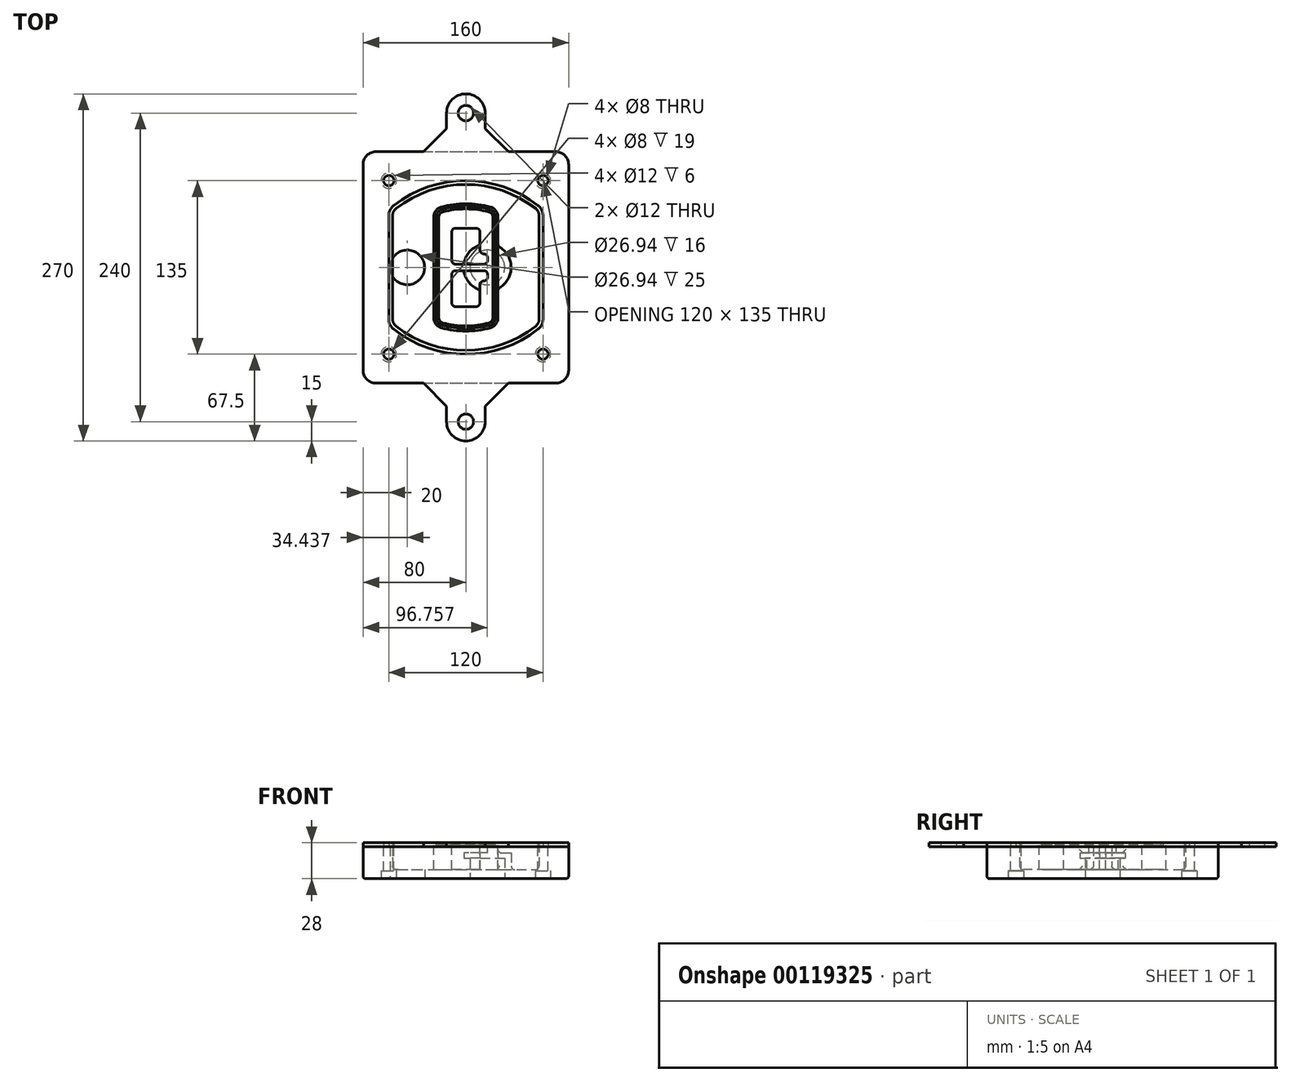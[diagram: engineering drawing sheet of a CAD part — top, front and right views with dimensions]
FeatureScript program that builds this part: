
annotation { "Feature Type Name" : "Feature", "Feature Type Description" : "" }
export const myFeature = defineFeature(function(context is Context, id is Id, definition is map)
    precondition{}
    {
        {
            var Q0;
            Q0=qCreatedBy(makeId("Top.planeOp"),FACE);
            var sketch = newSketch(context, id + "F0", { "sketchPlane" : qUnion([Q0])});
            skPoint(sketch, "E0.rect.middle", {"position": v(0, 0) * mm});
            skLineSegment(sketch, "E1.bottom", {"start": v(-70, -90) * mm, "end": v(70, -90) * mm});
            skLineSegment(sketch, "E1.top", {"start": v(-70, 90) * mm, "end": v(70, 90) * mm});
            skLineSegment(sketch, "E1.left", {"start": v(-80, -80) * mm, "end": v(-80, 80) * mm});
            skLineSegment(sketch, "E1.right", {"start": v(80, -80) * mm, "end": v(80, 80) * mm});
            skLineSegment(sketch, "E2", {"start": v(-80, 90) * mm, "end": v(80, -90) * mm, "construction": true});
            skLineSegment(sketch, "E3", {"start": v(80, 90) * mm, "end": v(-80, -90) * mm, "construction": true});
            skCircle(sketch, "E4", {"center": v(-60, 67.5) * mm, "radius": 4 * mm});
            skCircle(sketch, "E5", {"center": v(60, 67.5) * mm, "radius": 4 * mm});
            skCircle(sketch, "E6", {"center": v(60, -67.5) * mm, "radius": 4 * mm});
            skCircle(sketch, "E7", {"center": v(-60, -67.5) * mm, "radius": 4 * mm});
            skLineSegment(sketch, "E8", {"start": v(-60, 67.5) * mm, "end": v(60, 67.5) * mm, "construction": true});
            skLineSegment(sketch, "E9", {"start": v(60, 67.5) * mm, "end": v(60, -67.5) * mm, "construction": true});
            skLineSegment(sketch, "E10", {"start": v(60, -67.5) * mm, "end": v(-60, -67.5) * mm, "construction": true});
            skLineSegment(sketch, "E11", {"start": v(-60, -67.5) * mm, "end": v(-60, 67.5) * mm, "construction": true});
            skLineSegment(sketch, "E12", {"start": v(-60, 40.3) * mm, "end": v(-60, -40.3) * mm});
            skLineSegment(sketch, "E13", {"start": v(60, 40.3) * mm, "end": v(60, -40.3) * mm});
            skArc(sketch, "E14", {"start": v(56.15, 48.18) * mm, "mid": v(0, 67.5) * mm, "end": v(-56.15, 48.18) * mm});
            skArc(sketch, "E15", {"start": v(-56.15, -48.18) * mm, "mid": v(0, -67.5) * mm, "end": v(56.15, -48.18) * mm});
            skLineSegment(sketch, "E16", {"start": v(-60, 0) * mm, "end": v(60, 0) * mm, "construction": true});
            skPoint(sketch, "E17.visualSharp", {"position": v(-60, -45) * mm});
            skArc(sketch, "E17.filletArc", {"start": v(-60, -40.3) * mm, "mid": v(-58.99, -44.68) * mm, "end": v(-56.15, -48.18) * mm});
            skPoint(sketch, "E18.visualSharp", {"position": v(-60, 45) * mm});
            skArc(sketch, "E18.filletArc", {"start": v(-56.15, 48.18) * mm, "mid": v(-58.99, 44.68) * mm, "end": v(-60, 40.3) * mm});
            skPoint(sketch, "E19.visualSharp", {"position": v(60, 45) * mm});
            skArc(sketch, "E19.filletArc", {"start": v(60, 40.3) * mm, "mid": v(58.99, 44.68) * mm, "end": v(56.15, 48.18) * mm});
            skPoint(sketch, "E20.visualSharp", {"position": v(60, -45) * mm});
            skArc(sketch, "E20.filletArc", {"start": v(56.15, -48.18) * mm, "mid": v(58.99, -44.68) * mm, "end": v(60, -40.3) * mm});
            skPoint(sketch, "E21.visualSharp", {"position": v(-80, 90) * mm});
            skArc(sketch, "E21.filletArc", {"start": v(-70, 90) * mm, "mid": v(-77.07, 87.07) * mm, "end": v(-80, 80) * mm});
            skPoint(sketch, "E22.visualSharp", {"position": v(80, 90) * mm});
            skArc(sketch, "E22.filletArc", {"start": v(80, 80) * mm, "mid": v(77.07, 87.07) * mm, "end": v(70, 90) * mm});
            skPoint(sketch, "E23.visualSharp", {"position": v(80, -90) * mm});
            skArc(sketch, "E23.filletArc", {"start": v(70, -90) * mm, "mid": v(77.07, -87.07) * mm, "end": v(80, -80) * mm});
            skPoint(sketch, "E24.visualSharp", {"position": v(-80, -90) * mm});
            skArc(sketch, "E24.filletArc", {"start": v(-80, -80) * mm, "mid": v(-77.07, -87.07) * mm, "end": v(-70, -90) * mm});
            skArc(sketch, "E25.0", {"start": v(57, 40.3) * mm, "mid": v(56.3, 43.36) * mm, "end": v(54.3, 45.81) * mm});
            skLineSegment(sketch, "E25.1", {"start": v(57, 40.3) * mm, "end": v(57, -40.3) * mm});
            skArc(sketch, "E25.2", {"start": v(54.3, -45.81) * mm, "mid": v(56.3, -43.36) * mm, "end": v(57, -40.3) * mm});
            skArc(sketch, "E25.3", {"start": v(-54.3, -45.81) * mm, "mid": v(0, -64.5) * mm, "end": v(54.3, -45.81) * mm});
            skArc(sketch, "E25.4", {"start": v(-57, -40.3) * mm, "mid": v(-56.3, -43.36) * mm, "end": v(-54.3, -45.81) * mm});
            skArc(sketch, "E25.5", {"start": v(54.3, 45.81) * mm, "mid": v(0, 64.5) * mm, "end": v(-54.3, 45.81) * mm});
            skLineSegment(sketch, "E25.6", {"start": v(-57, 40.3) * mm, "end": v(-57, -40.3) * mm});
            skArc(sketch, "E25.7", {"start": v(-54.3, 45.81) * mm, "mid": v(-56.3, 43.36) * mm, "end": v(-57, 40.3) * mm});
            skArc(sketch, "E26.0", {"start": v(-58.62, 51.33) * mm, "mid": v(-62.58, 46.43) * mm, "end": v(-64, 40.3) * mm});
            skArc(sketch, "E26.1", {"start": v(58.62, 51.33) * mm, "mid": v(0, 71.5) * mm, "end": v(-58.62, 51.33) * mm});
            skArc(sketch, "E26.2", {"start": v(64, 40.3) * mm, "mid": v(62.58, 46.43) * mm, "end": v(58.62, 51.33) * mm});
            skLineSegment(sketch, "E26.3", {"start": v(64, 40.3) * mm, "end": v(64, -40.3) * mm});
            skArc(sketch, "E26.4", {"start": v(58.62, -51.33) * mm, "mid": v(62.58, -46.43) * mm, "end": v(64, -40.3) * mm});
            skLineSegment(sketch, "E26.5", {"start": v(-64, 40.3) * mm, "end": v(-64, -40.3) * mm});
            skArc(sketch, "E26.6", {"start": v(-58.62, -51.33) * mm, "mid": v(0, -71.5) * mm, "end": v(58.62, -51.33) * mm});
            skArc(sketch, "E26.7", {"start": v(-64, -40.3) * mm, "mid": v(-62.58, -46.43) * mm, "end": v(-58.62, -51.33) * mm});
            skSolve(sketch);
        }
        {
            var Q0;
            Q0=makeQuery(id+"F0.imprint","IMPRINT",FACE,{"disambiguationData":[TD([[makeQuery(id+"F0.imprint","IMPRINT",EDGE,{"derivedFrom":sQuery(id+"F0.wireOp",EDGE,"E1.bottom")}),1.0]])]});
            var Q1;
            Q1=makeQuery(id+"F0.imprint","IMPRINT",FACE,{"disambiguationData":[TD([[makeQuery(id+"F0.imprint","IMPRINT",EDGE,{"derivedFrom":sQuery(id+"F0.wireOp",EDGE,"E12")}),1.0]])]});
            var Q2;
            Q2=makeQuery(id+"F0.imprint","IMPRINT",FACE,{"disambiguationData":[TD([[makeQuery(id+"F0.imprint","IMPRINT",EDGE,{"derivedFrom":sQuery(id+"F0.wireOp",EDGE,"E25.0")}),1.0]])]});
            var Q3;
            Q3=makeQuery(id+"F0.imprint","IMPRINT",FACE,{"disambiguationData":[TD([[makeQuery(id+"F0.imprint","IMPRINT",EDGE,{"derivedFrom":sQuery(id+"F0.wireOp",EDGE,"E12")}),-1.0]])]});
            extrude(context, id + "F1", {"entities" : qUnion([Q0, Q1, Q2, Q3]), "oppositeDirection" : true, "depth" : 25 * mm});
        }
        {
            var Q0;
            Q0=makeQuery(id+"F0.imprint","IMPRINT",FACE,{"disambiguationData":[TD([[makeQuery(id+"F0.imprint","IMPRINT",EDGE,{"derivedFrom":sQuery(id+"F0.wireOp",EDGE,"E12")}),1.0]])]});
            extrude(context, id + "F2", {"entities" : qUnion([Q0]), "operationType" : NewBodyOperationType.ADD, "depth" : 3 * mm});
        }
        {
            var Q0;
            Q0=makeQuery(id+"F0.imprint","IMPRINT",FACE,{"disambiguationData":[TD([[makeQuery(id+"F0.imprint","IMPRINT",EDGE,{"derivedFrom":sQuery(id+"F0.wireOp",EDGE,"E25.0")}),1.0]])]});
            extrude(context, id + "F3", {"entities" : qUnion([Q0]), "operationType" : NewBodyOperationType.REMOVE, "oppositeDirection" : true, "depth" : 18 * mm});
        }
        {
            var Q0;
            Q0=makeQuery(id+"F2.opExtrude","CAP_FACE",FACE,{"disambiguationData":[OSD([sQuery(id+"F0.wireOp",EDGE,"E12"),sQuery(id+"F0.wireOp",EDGE,"E13"),sQuery(id+"F0.wireOp",EDGE,"E14"),sQuery(id+"F0.wireOp",EDGE,"E15"),sQuery(id+"F0.wireOp",EDGE,"E17.filletArc"),sQuery(id+"F0.wireOp",EDGE,"E18.filletArc"),sQuery(id+"F0.wireOp",EDGE,"E19.filletArc"),sQuery(id+"F0.wireOp",EDGE,"E20.filletArc"),sQuery(id+"F0.wireOp",EDGE,"E25.0"),sQuery(id+"F0.wireOp",EDGE,"E25.1"),sQuery(id+"F0.wireOp",EDGE,"E25.2"),sQuery(id+"F0.wireOp",EDGE,"E25.3"),sQuery(id+"F0.wireOp",EDGE,"E25.4"),sQuery(id+"F0.wireOp",EDGE,"E25.5"),sQuery(id+"F0.wireOp",EDGE,"E25.6"),sQuery(id+"F0.wireOp",EDGE,"E25.7")])],"isStart":false});
            var sketch = newSketch(context, id + "F4", { "sketchPlane" : qUnion([Q0])});
            skArc(sketch, "E27.0", {"start": v(-19.08, -46.97) * mm, "mid": v(0, -49.5) * mm, "end": v(19.08, -46.97) * mm});
            skArc(sketch, "E28.0", {"start": v(19.08, 46.97) * mm, "mid": v(0, 49.5) * mm, "end": v(-19.08, 46.97) * mm});
            skLineSegment(sketch, "E29", {"start": v(-25, 39.25) * mm, "end": v(-25, -39.25) * mm});
            skLineSegment(sketch, "E30", {"start": v(25, 39.25) * mm, "end": v(25, -39.25) * mm});
            skLineSegment(sketch, "E31", {"start": v(-25, 45.1) * mm, "end": v(25, 45.1) * mm, "construction": true});
            skLineSegment(sketch, "E32", {"start": v(-25, -45.1) * mm, "end": v(25, -45.1) * mm, "construction": true});
            skPoint(sketch, "E33.visualSharp", {"position": v(-25, 45.1) * mm});
            skArc(sketch, "E33.filletArc", {"start": v(-19.08, 46.97) * mm, "mid": v(-23.35, 44.11) * mm, "end": v(-25, 39.25) * mm});
            skPoint(sketch, "E34.visualSharp", {"position": v(25, 45.1) * mm});
            skArc(sketch, "E34.filletArc", {"start": v(25, 39.25) * mm, "mid": v(23.35, 44.11) * mm, "end": v(19.08, 46.97) * mm});
            skPoint(sketch, "E35.visualSharp", {"position": v(25, -45.1) * mm});
            skArc(sketch, "E35.filletArc", {"start": v(19.08, -46.97) * mm, "mid": v(23.35, -44.11) * mm, "end": v(25, -39.25) * mm});
            skPoint(sketch, "E36.visualSharp", {"position": v(-25, -45.1) * mm});
            skArc(sketch, "E36.filletArc", {"start": v(-25, -39.25) * mm, "mid": v(-23.35, -44.11) * mm, "end": v(-19.08, -46.97) * mm});
            skArc(sketch, "E37.0", {"start": v(54.3, 45.81) * mm, "mid": v(0, 64.5) * mm, "end": v(-54.3, 45.81) * mm});
            skArc(sketch, "E37.1", {"start": v(-54.3, 45.81) * mm, "mid": v(-56.3, 43.36) * mm, "end": v(-57, 40.3) * mm});
            skLineSegment(sketch, "E37.2", {"start": v(-57, 40.3) * mm, "end": v(-57, -40.3) * mm});
            skArc(sketch, "E37.3", {"start": v(-57, -40.3) * mm, "mid": v(-56.3, -43.36) * mm, "end": v(-54.3, -45.81) * mm});
            skArc(sketch, "E37.4", {"start": v(-54.3, -45.81) * mm, "mid": v(0, -64.5) * mm, "end": v(54.3, -45.81) * mm});
            skArc(sketch, "E37.5", {"start": v(54.3, -45.81) * mm, "mid": v(56.3, -43.36) * mm, "end": v(57, -40.3) * mm});
            skLineSegment(sketch, "E37.6", {"start": v(57, 40.3) * mm, "end": v(57, -40.3) * mm});
            skArc(sketch, "E37.7", {"start": v(57, 40.3) * mm, "mid": v(56.3, 43.36) * mm, "end": v(54.3, 45.81) * mm});
            skLineSegment(sketch, "E38.0", {"start": v(23, 39.25) * mm, "end": v(23, -39.25) * mm});
            skArc(sketch, "E38.1", {"start": v(18.56, -45.04) * mm, "mid": v(21.76, -42.9) * mm, "end": v(23, -39.25) * mm});
            skArc(sketch, "E38.2", {"start": v(-18.56, -45.04) * mm, "mid": v(0, -47.5) * mm, "end": v(18.56, -45.04) * mm});
            skArc(sketch, "E38.3", {"start": v(-23, -39.25) * mm, "mid": v(-21.76, -42.9) * mm, "end": v(-18.56, -45.04) * mm});
            skLineSegment(sketch, "E38.4", {"start": v(-23, 39.25) * mm, "end": v(-23, -39.25) * mm});
            skArc(sketch, "E38.5", {"start": v(23, 39.25) * mm, "mid": v(21.76, 42.9) * mm, "end": v(18.56, 45.04) * mm});
            skArc(sketch, "E38.6", {"start": v(-18.56, 45.04) * mm, "mid": v(-21.76, 42.9) * mm, "end": v(-23, 39.25) * mm});
            skArc(sketch, "E38.7", {"start": v(18.56, 45.04) * mm, "mid": v(0, 47.5) * mm, "end": v(-18.56, 45.04) * mm});
            skArc(sketch, "E39.0", {"start": v(21, 39.25) * mm, "mid": v(20.18, 41.68) * mm, "end": v(18.04, 43.1) * mm});
            skLineSegment(sketch, "E39.1", {"start": v(21, 39.25) * mm, "end": v(21, -39.25) * mm});
            skArc(sketch, "E39.2", {"start": v(18.04, -43.1) * mm, "mid": v(20.18, -41.68) * mm, "end": v(21, -39.25) * mm});
            skArc(sketch, "E39.3", {"start": v(-18.04, -43.1) * mm, "mid": v(0, -45.5) * mm, "end": v(18.04, -43.1) * mm});
            skArc(sketch, "E39.4", {"start": v(-21, -39.25) * mm, "mid": v(-20.18, -41.68) * mm, "end": v(-18.04, -43.1) * mm});
            skArc(sketch, "E39.5", {"start": v(18.04, 43.1) * mm, "mid": v(0, 45.5) * mm, "end": v(-18.04, 43.1) * mm});
            skLineSegment(sketch, "E39.6", {"start": v(-21, 39.25) * mm, "end": v(-21, -39.25) * mm});
            skArc(sketch, "E39.7", {"start": v(-18.04, 43.1) * mm, "mid": v(-20.18, 41.68) * mm, "end": v(-21, 39.25) * mm});
            skLineSegment(sketch, "E40", {"start": v(-25, 0) * mm, "end": v(25, 0) * mm, "construction": true});
            skLineSegment(sketch, "E41", {"start": v(-11, 5.5) * mm, "end": v(-11, 27.5) * mm});
            skLineSegment(sketch, "E42", {"start": v(-8, 30.5) * mm, "end": v(8, 30.5) * mm});
            skLineSegment(sketch, "E43", {"start": v(11, 27.5) * mm, "end": v(11, 13.5) * mm});
            skLineSegment(sketch, "E44", {"start": v(14, 10.5) * mm, "end": v(14, 10.5) * mm});
            skLineSegment(sketch, "E45", {"start": v(17, 7.5) * mm, "end": v(17, 5.5) * mm});
            skLineSegment(sketch, "E46", {"start": v(14, 2.5) * mm, "end": v(-8, 2.5) * mm});
            skPoint(sketch, "E47.visualSharp", {"position": v(-11, 30.5) * mm});
            skArc(sketch, "E47.filletArc", {"start": v(-8, 30.5) * mm, "mid": v(-10.12, 29.62) * mm, "end": v(-11, 27.5) * mm});
            skPoint(sketch, "E48.visualSharp", {"position": v(11, 30.5) * mm});
            skArc(sketch, "E48.filletArc", {"start": v(11, 27.5) * mm, "mid": v(10.12, 29.62) * mm, "end": v(8, 30.5) * mm});
            skPoint(sketch, "E49.visualSharp", {"position": v(11, 10.5) * mm});
            skArc(sketch, "E49.filletArc", {"start": v(11, 13.5) * mm, "mid": v(11.88, 11.38) * mm, "end": v(14, 10.5) * mm});
            skPoint(sketch, "E50.visualSharp", {"position": v(17, 10.5) * mm});
            skArc(sketch, "E50.filletArc", {"start": v(17, 7.5) * mm, "mid": v(16.12, 9.62) * mm, "end": v(14, 10.5) * mm});
            skPoint(sketch, "E51.visualSharp", {"position": v(17, 2.5) * mm});
            skArc(sketch, "E51.filletArc", {"start": v(14, 2.5) * mm, "mid": v(16.12, 3.38) * mm, "end": v(17, 5.5) * mm});
            skPoint(sketch, "E52.visualSharp", {"position": v(-11, 2.5) * mm});
            skArc(sketch, "E52.filletArc", {"start": v(-11, 5.5) * mm, "mid": v(-10.12, 3.38) * mm, "end": v(-8, 2.5) * mm});
            skLineSegment(sketch, "E53.0.MirrorCS", {"start": v(14, -2.5) * mm, "end": v(-8, -2.5) * mm});
            skArc(sketch, "E54.0.MirrorCS", {"start": v(-11, -5.5) * mm, "mid": v(-10.12, -3.38) * mm, "end": v(-8, -2.5) * mm});
            skLineSegment(sketch, "E55.0.MirrorCS", {"start": v(-11, -5.5) * mm, "end": v(-11, -27.5) * mm});
            skArc(sketch, "E56.0.MirrorCS", {"start": v(-8, -30.5) * mm, "mid": v(-10.12, -29.62) * mm, "end": v(-11, -27.5) * mm});
            skLineSegment(sketch, "E57.0.MirrorCS", {"start": v(-8, -30.5) * mm, "end": v(8, -30.5) * mm});
            skArc(sketch, "E58.0.MirrorCS", {"start": v(11, -27.5) * mm, "mid": v(10.12, -29.62) * mm, "end": v(8, -30.5) * mm});
            skLineSegment(sketch, "E59.0.MirrorCS", {"start": v(11, -27.5) * mm, "end": v(11, -13.5) * mm});
            skArc(sketch, "E60.0.MirrorCS", {"start": v(11, -13.5) * mm, "mid": v(11.88, -11.38) * mm, "end": v(14, -10.5) * mm});
            skArc(sketch, "E61.0.MirrorCS", {"start": v(17, -7.5) * mm, "mid": v(16.12, -9.62) * mm, "end": v(14, -10.5) * mm});
            skLineSegment(sketch, "E62.0.MirrorCS", {"start": v(17, -7.5) * mm, "end": v(17, -5.5) * mm});
            skArc(sketch, "E63.0.MirrorCS", {"start": v(14, -2.5) * mm, "mid": v(16.12, -3.38) * mm, "end": v(17, -5.5) * mm});
            skSolve(sketch);
        }
        {
            var Q0;
            Q0=makeQuery(id+"F4.imprint","IMPRINT",FACE,{"disambiguationData":[TD([[makeQuery(id+"F4.imprint","IMPRINT",EDGE,{"derivedFrom":sQuery(id+"F4.wireOp",EDGE,"E27.0")}),1.0]])]});
            var Q1;
            Q1=makeQuery(id+"F4.imprint","IMPRINT",FACE,{"disambiguationData":[TD([[makeQuery(id+"F4.imprint","IMPRINT",EDGE,{"derivedFrom":sQuery(id+"F4.wireOp",EDGE,"E38.0")}),-1.0]])]});
            var Q2;
            Q2=makeQuery(id+"F4.imprint","IMPRINT",FACE,{"disambiguationData":[TD([[makeQuery(id+"F4.imprint","IMPRINT",EDGE,{"derivedFrom":sQuery(id+"F4.wireOp",EDGE,"E39.0")}),1.0]])]});
            extrude(context, id + "F5", {"entities" : qUnion([Q0, Q1, Q2]), "operationType" : NewBodyOperationType.ADD, "endBound" : BoundingType.UP_TO_NEXT, "oppositeDirection" : true, "depth" : 25 * mm});
        }
        {
            var Q0;
            Q0=makeQuery(id+"F4.imprint","IMPRINT",FACE,{"disambiguationData":[TD([[makeQuery(id+"F4.imprint","IMPRINT",EDGE,{"derivedFrom":sQuery(id+"F4.wireOp",EDGE,"E38.0")}),-1.0]])]});
            extrude(context, id + "F6", {"entities" : qUnion([Q0]), "operationType" : NewBodyOperationType.REMOVE, "oppositeDirection" : true, "depth" : 2 * mm});
        }
        {
            var Q0;
            Q0=makeQuery(id+"F1.opExtrude","CAP_FACE",FACE,{"disambiguationData":[OSD([sQuery(id+"F0.wireOp",EDGE,"E1.bottom"),sQuery(id+"F0.wireOp",EDGE,"E1.top"),sQuery(id+"F0.wireOp",EDGE,"E1.left"),sQuery(id+"F0.wireOp",EDGE,"E1.right"),sQuery(id+"F0.wireOp",EDGE,"E4"),sQuery(id+"F0.wireOp",EDGE,"E5"),sQuery(id+"F0.wireOp",EDGE,"E6"),sQuery(id+"F0.wireOp",EDGE,"E7"),sQuery(id+"F0.wireOp",EDGE,"E21.filletArc"),sQuery(id+"F0.wireOp",EDGE,"E22.filletArc"),sQuery(id+"F0.wireOp",EDGE,"E23.filletArc"),sQuery(id+"F0.wireOp",EDGE,"E24.filletArc")])],"isStart":false});
            var sketch = newSketch(context, id + "F7", { "sketchPlane" : qUnion([Q0])});
            skCircle(sketch, "E64", {"center": v(16.76, 0) * mm, "radius": 13.47 * mm});
            skCircle(sketch, "E65", {"center": v(-45.56, 0) * mm, "radius": 13.47 * mm});
            skLineSegment(sketch, "E66", {"start": v(80, 0) * mm, "end": v(-80, 0) * mm});
            skCircle(sketch, "E67", {"center": v(16.76, 0) * mm, "radius": 18.47 * mm});
            skCircle(sketch, "E68", {"center": v(60, -67.5) * mm, "radius": 6 * mm});
            skCircle(sketch, "E69", {"center": v(-60, -67.5) * mm, "radius": 6 * mm});
            skCircle(sketch, "E70", {"center": v(-60, 67.5) * mm, "radius": 6 * mm});
            skCircle(sketch, "E71", {"center": v(60, 67.5) * mm, "radius": 6 * mm});
            skSolve(sketch);
        }
        {
            var Q0;
            {var subQ1=sQuery(id+"F7.wireOp",EDGE,"E66");var subQ4=sQuery(id+"F7.wireOp",EDGE,"E64");var subQ6=makeQuery(id+"F7.imprint","INTERSECT",VERTEX,{"disambiguationData":[OD(0.0)],"derivedFrom":[subQ4,subQ1]});Q0=makeQuery(id+"F7.imprint","IMPRINT",FACE,{"disambiguationData":[TD([[makeQuery(id+"F7.imprint","IMPRINT",EDGE,{"disambiguationData":[TD([[subQ6,-1.0]])],"derivedFrom":subQ4}),-1.0]])]});}
            var Q1;
            {var subQ0=sQuery(id+"F7.wireOp",EDGE,"E66");var subQ1=sQuery(id+"F7.wireOp",EDGE,"E64");var subQ3=makeQuery(id+"F7.imprint","INTERSECT",VERTEX,{"disambiguationData":[OD(0.0)],"derivedFrom":[subQ1,subQ0]});Q1=makeQuery(id+"F7.imprint","IMPRINT",FACE,{"disambiguationData":[TD([[makeQuery(id+"F7.imprint","IMPRINT",EDGE,{"disambiguationData":[TD([[subQ3,-1.0]])],"derivedFrom":subQ1}),1.0]])]});}
            var Q2;
            {var subQ0=sQuery(id+"F7.wireOp",EDGE,"E66");var subQ1=sQuery(id+"F7.wireOp",EDGE,"E64");var subQ3=makeQuery(id+"F7.imprint","INTERSECT",VERTEX,{"disambiguationData":[OD(0.0)],"derivedFrom":[subQ1,subQ0]});Q2=makeQuery(id+"F7.imprint","IMPRINT",FACE,{"disambiguationData":[TD([[makeQuery(id+"F7.imprint","IMPRINT",EDGE,{"disambiguationData":[TD([[subQ3,1.0]])],"derivedFrom":subQ1}),1.0]])]});}
            var Q3;
            {var subQ1=sQuery(id+"F7.wireOp",EDGE,"E66");var subQ4=sQuery(id+"F7.wireOp",EDGE,"E64");var subQ6=makeQuery(id+"F7.imprint","INTERSECT",VERTEX,{"disambiguationData":[OD(0.0)],"derivedFrom":[subQ4,subQ1]});Q3=makeQuery(id+"F7.imprint","IMPRINT",FACE,{"disambiguationData":[TD([[makeQuery(id+"F7.imprint","IMPRINT",EDGE,{"disambiguationData":[TD([[subQ6,1.0]])],"derivedFrom":subQ4}),-1.0]])]});}
            extrude(context, id + "F8", {"entities" : qUnion([Q0, Q1, Q2, Q3]), "operationType" : NewBodyOperationType.ADD, "oppositeDirection" : true, "depth" : 20 * mm});
        }
        {
            var Q0;
            {var subQ0=sQuery(id+"F7.wireOp",EDGE,"E66");var subQ1=sQuery(id+"F7.wireOp",EDGE,"E64");var subQ3=makeQuery(id+"F7.imprint","INTERSECT",VERTEX,{"disambiguationData":[OD(0.0)],"derivedFrom":[subQ1,subQ0]});Q0=makeQuery(id+"F7.imprint","IMPRINT",FACE,{"disambiguationData":[TD([[makeQuery(id+"F7.imprint","IMPRINT",EDGE,{"disambiguationData":[TD([[subQ3,-1.0]])],"derivedFrom":subQ1}),1.0]])]});}
            var Q1;
            {var subQ0=sQuery(id+"F7.wireOp",EDGE,"E66");var subQ1=sQuery(id+"F7.wireOp",EDGE,"E64");var subQ3=makeQuery(id+"F7.imprint","INTERSECT",VERTEX,{"disambiguationData":[OD(0.0)],"derivedFrom":[subQ1,subQ0]});Q1=makeQuery(id+"F7.imprint","IMPRINT",FACE,{"disambiguationData":[TD([[makeQuery(id+"F7.imprint","IMPRINT",EDGE,{"disambiguationData":[TD([[subQ3,1.0]])],"derivedFrom":subQ1}),1.0]])]});}
            extrude(context, id + "F9", {"entities" : qUnion([Q0, Q1]), "operationType" : NewBodyOperationType.REMOVE, "oppositeDirection" : true, "depth" : 16 * mm});
        }
        {
            var Q0;
            {var subQ0=sQuery(id+"F7.wireOp",EDGE,"E66");var subQ1=sQuery(id+"F7.wireOp",EDGE,"E65");var subQ3=makeQuery(id+"F7.imprint","INTERSECT",VERTEX,{"disambiguationData":[OD(0.0)],"derivedFrom":[subQ1,subQ0]});Q0=makeQuery(id+"F7.imprint","IMPRINT",FACE,{"disambiguationData":[TD([[makeQuery(id+"F7.imprint","IMPRINT",EDGE,{"disambiguationData":[TD([[subQ3,-1.0]])],"derivedFrom":subQ1}),1.0]])]});}
            var Q1;
            {var subQ0=sQuery(id+"F7.wireOp",EDGE,"E66");var subQ1=sQuery(id+"F7.wireOp",EDGE,"E65");var subQ3=makeQuery(id+"F7.imprint","INTERSECT",VERTEX,{"disambiguationData":[OD(0.0)],"derivedFrom":[subQ1,subQ0]});Q1=makeQuery(id+"F7.imprint","IMPRINT",FACE,{"disambiguationData":[TD([[makeQuery(id+"F7.imprint","IMPRINT",EDGE,{"disambiguationData":[TD([[subQ3,1.0]])],"derivedFrom":subQ1}),1.0]])]});}
            extrude(context, id + "F10", {"entities" : qUnion([Q0, Q1]), "operationType" : NewBodyOperationType.REMOVE, "oppositeDirection" : true, "depth" : 25 * mm});
        }
        {
            var Q0;
            Q0=makeQuery(id+"F7.imprint","IMPRINT",FACE,{"disambiguationData":[TD([[makeQuery(id+"F7.imprint","IMPRINT",EDGE,{"derivedFrom":sQuery(id+"F7.wireOp",EDGE,"E68")}),1.0]])]});
            var Q1;
            Q1=makeQuery(id+"F7.imprint","IMPRINT",FACE,{"disambiguationData":[TD([[makeQuery(id+"F7.imprint","IMPRINT",EDGE,{"derivedFrom":makeQuery(id+"F1.opExtrude","CAP_EDGE",EDGE,{"disambiguationData":[OSD([sQuery(id+"F0.wireOp",EDGE,"E5")])],"isStart":false})}),-1.0]])]});
            var Q2;
            Q2=makeQuery(id+"F7.imprint","IMPRINT",FACE,{"disambiguationData":[TD([[makeQuery(id+"F7.imprint","IMPRINT",EDGE,{"derivedFrom":sQuery(id+"F7.wireOp",EDGE,"E69")}),1.0]])]});
            var Q3;
            Q3=makeQuery(id+"F7.imprint","IMPRINT",FACE,{"disambiguationData":[TD([[makeQuery(id+"F7.imprint","IMPRINT",EDGE,{"derivedFrom":makeQuery(id+"F1.opExtrude","CAP_EDGE",EDGE,{"disambiguationData":[OSD([sQuery(id+"F0.wireOp",EDGE,"E4")])],"isStart":false})}),-1.0]])]});
            var Q4;
            Q4=makeQuery(id+"F7.imprint","IMPRINT",FACE,{"disambiguationData":[TD([[makeQuery(id+"F7.imprint","IMPRINT",EDGE,{"derivedFrom":sQuery(id+"F7.wireOp",EDGE,"E70")}),1.0]])]});
            var Q5;
            Q5=makeQuery(id+"F7.imprint","IMPRINT",FACE,{"disambiguationData":[TD([[makeQuery(id+"F7.imprint","IMPRINT",EDGE,{"derivedFrom":makeQuery(id+"F1.opExtrude","CAP_EDGE",EDGE,{"disambiguationData":[OSD([sQuery(id+"F0.wireOp",EDGE,"E7")])],"isStart":false})}),-1.0]])]});
            var Q6;
            Q6=makeQuery(id+"F7.imprint","IMPRINT",FACE,{"disambiguationData":[TD([[makeQuery(id+"F7.imprint","IMPRINT",EDGE,{"derivedFrom":sQuery(id+"F7.wireOp",EDGE,"E71")}),1.0]])]});
            var Q7;
            Q7=makeQuery(id+"F7.imprint","IMPRINT",FACE,{"disambiguationData":[TD([[makeQuery(id+"F7.imprint","IMPRINT",EDGE,{"derivedFrom":makeQuery(id+"F1.opExtrude","CAP_EDGE",EDGE,{"disambiguationData":[OSD([sQuery(id+"F0.wireOp",EDGE,"E6")])],"isStart":false})}),-1.0]])]});
            extrude(context, id + "F11", {"entities" : qUnion([Q0, Q1, Q2, Q3, Q4, Q5, Q6, Q7]), "operationType" : NewBodyOperationType.REMOVE, "oppositeDirection" : true, "depth" : 6 * mm});
        }
        {
            var Q0;
            Q0=makeQuery(id+"F9.boolean.opBoolean","COPY",FACE,{"derivedFrom":makeQuery(id+"F9.opExtrude","CAP_FACE",FACE,{"disambiguationData":[OSD([sQuery(id+"F7.wireOp",EDGE,"E64")])],"isStart":false})});
            var sketch = newSketch(context, id + "F12", { "sketchPlane" : qUnion([Q0])});
            skArc(sketch, "E72.0", {"start": v(11, 17.55) * mm, "mid": v(2.57, 11.82) * mm, "end": v(-1.54, 2.5) * mm});
            skArc(sketch, "E72.1", {"start": v(-1.54, -2.5) * mm, "mid": v(2.57, -11.82) * mm, "end": v(11, -17.55) * mm});
            skLineSegment(sketch, "E73", {"start": v(-1.54, -2.5) * mm, "end": v(14, -2.5) * mm});
            skLineSegment(sketch, "E74.0", {"start": v(14, 2.5) * mm, "end": v(-1.54, 2.5) * mm});
            skArc(sketch, "E74.1", {"start": v(14, 2.5) * mm, "mid": v(16.12, 3.38) * mm, "end": v(17, 5.5) * mm});
            skLineSegment(sketch, "E74.2", {"start": v(17, 7.5) * mm, "end": v(17, 5.5) * mm});
            skArc(sketch, "E74.3", {"start": v(17, 7.5) * mm, "mid": v(16.12, 9.62) * mm, "end": v(14, 10.5) * mm});
            skArc(sketch, "E74.4", {"start": v(11, 13.5) * mm, "mid": v(11.88, 11.38) * mm, "end": v(14, 10.5) * mm});
            skLineSegment(sketch, "E74.5", {"start": v(11, 17.55) * mm, "end": v(11, 13.5) * mm});
            skLineSegment(sketch, "E74.7", {"start": v(14, -2.5) * mm, "end": v(-1.54, -2.5) * mm});
            skArc(sketch, "E74.8", {"start": v(14, -2.5) * mm, "mid": v(16.12, -3.38) * mm, "end": v(17, -5.5) * mm});
            skLineSegment(sketch, "E74.9", {"start": v(17, -7.5) * mm, "end": v(17, -5.5) * mm});
            skArc(sketch, "E74.10", {"start": v(17, -7.5) * mm, "mid": v(16.12, -9.62) * mm, "end": v(14, -10.5) * mm});
            skArc(sketch, "E74.11", {"start": v(11, -13.5) * mm, "mid": v(11.88, -11.38) * mm, "end": v(14, -10.5) * mm});
            skLineSegment(sketch, "E74.12", {"start": v(11, -17.55) * mm, "end": v(11, -13.5) * mm});
            skPoint(sketch, "E75.orphan", {"position": v(11, -27.5) * mm});
            skPoint(sketch, "E76.orphan", {"position": v(-8, -2.5) * mm});
            skPoint(sketch, "E77.orphan", {"position": v(-8, 2.5) * mm});
            skPoint(sketch, "E78.orphan", {"position": v(11, 27.5) * mm});
            skSolve(sketch);
        }
        {
            var Q0;
            {var subQ7=sQuery(id+"F12.wireOp",EDGE,"E72.0");var subQ14=sQuery(id+"F12.wireOp",EDGE,"E72.1");var subQ16=sQuery(id+"F12.wireOp",EDGE,"E74.1");var subQ18=sQuery(id+"F12.wireOp",EDGE,"E74.8");Q0=qUnion([makeQuery(id+"F12.imprint","IMPRINT",FACE,{"disambiguationData":[TD([[makeQuery(id+"F12.imprint","IMPRINT",EDGE,{"derivedFrom":subQ7}),1.0]])]}),makeQuery(id+"F12.imprint","IMPRINT",FACE,{"disambiguationData":[TD([[makeQuery(id+"F12.imprint","IMPRINT",EDGE,{"derivedFrom":subQ14}),1.0]])]}),makeQuery(id+"F12.imprint","IMPRINT",FACE,{"disambiguationData":[TD([[makeQuery(id+"F12.imprint","IMPRINT",EDGE,{"derivedFrom":subQ16}),1.0]])]}),makeQuery(id+"F12.imprint","IMPRINT",FACE,{"disambiguationData":[TD([[makeQuery(id+"F12.imprint","IMPRINT",EDGE,{"derivedFrom":subQ18}),-1.0]])]})]);}
            var Q1;
            Q1=makeQuery(id+"F5.boolean.opBoolean","SPLIT",FACE,{"disambiguationData":[TD([makeQuery(id+"F5.opExtrude","SWEPT_FACE",FACE,{"disambiguationData":[OSD([sQuery(id+"F4.wireOp",EDGE,"E41")])]})])],"derivedFrom":makeQuery(id+"F3.boolean.opBoolean","COPY",FACE,{"derivedFrom":makeQuery(id+"F3.opExtrude","CAP_FACE",FACE,{"disambiguationData":[OSD([sQuery(id+"F0.wireOp",EDGE,"E25.0"),sQuery(id+"F0.wireOp",EDGE,"E25.1"),sQuery(id+"F0.wireOp",EDGE,"E25.2"),sQuery(id+"F0.wireOp",EDGE,"E25.3"),sQuery(id+"F0.wireOp",EDGE,"E25.4"),sQuery(id+"F0.wireOp",EDGE,"E25.5"),sQuery(id+"F0.wireOp",EDGE,"E25.6"),sQuery(id+"F0.wireOp",EDGE,"E25.7")])],"isStart":false})})});
            extrude(context, id + "F13", {"entities" : qUnion([Q0]), "operationType" : NewBodyOperationType.REMOVE, "endBound" : BoundingType.UP_TO_SURFACE, "endBoundEntityFace" : qUnion([Q1]), "depth" : 25 * mm});
        }
        {
            var Q0;
            Q0=makeQuery(id+"F3.boolean.opBoolean","COPY",EDGE,{"derivedFrom":makeQuery(id+"F3.opExtrude","CAP_EDGE",EDGE,{"disambiguationData":[OSD([sQuery(id+"F0.wireOp",EDGE,"E25.6")])],"isStart":false})});
            var Q1;
            Q1=makeQuery(id+"F8.boolean.opBoolean","INTERSECT",EDGE,{"derivedFrom":[makeQuery(id+"F5.opExtrude","SWEPT_FACE",FACE,{"disambiguationData":[OSD([sQuery(id+"F4.wireOp",EDGE,"E30")])]}),makeQuery(id+"F8.opExtrude","CAP_FACE",FACE,{"disambiguationData":[OSD([sQuery(id+"F7.wireOp",EDGE,"E67")])],"isStart":false})]});
            var Q2;
            Q2=makeQuery(id+"F8.boolean.opBoolean","INTERSECT",EDGE,{"disambiguationData":[OD(1.0)],"derivedFrom":[makeQuery(id+"F5.opExtrude","SWEPT_FACE",FACE,{"disambiguationData":[OSD([sQuery(id+"F4.wireOp",EDGE,"E30")])]}),makeQuery(id+"F8.opExtrude","SWEPT_FACE",FACE,{"disambiguationData":[OSD([sQuery(id+"F7.wireOp",EDGE,"E67")])]})]});
            var Q3;
            {var subQ0=makeQuery(id+"F3.boolean.opBoolean","COPY",FACE,{"derivedFrom":makeQuery(id+"F3.opExtrude","CAP_FACE",FACE,{"disambiguationData":[OSD([sQuery(id+"F0.wireOp",EDGE,"E25.0"),sQuery(id+"F0.wireOp",EDGE,"E25.1"),sQuery(id+"F0.wireOp",EDGE,"E25.2"),sQuery(id+"F0.wireOp",EDGE,"E25.3"),sQuery(id+"F0.wireOp",EDGE,"E25.4"),sQuery(id+"F0.wireOp",EDGE,"E25.5"),sQuery(id+"F0.wireOp",EDGE,"E25.6"),sQuery(id+"F0.wireOp",EDGE,"E25.7")])],"isStart":false})});var subQ1=sQuery(id+"F4.wireOp",EDGE,"E30");Q3=makeQuery(id+"F8.boolean.opBoolean","SPLIT",EDGE,{"disambiguationData":[TD([makeQuery(id+"F5.opExtrude","SWEPT_FACE",FACE,{"disambiguationData":[OSD([sQuery(id+"F4.wireOp",EDGE,"E35.filletArc")])]})])],"derivedFrom":makeQuery(id+"F5.opExtrude","TWEAK_EDGE",EDGE,{"derivedFrom":[subQ0,makeQuery(id+"F4.imprint","IMPRINT",EDGE,{"derivedFrom":subQ1})]})});}
            var Q4;
            {var subQ0=sQuery(id+"F0.wireOp",EDGE,"E25.0");var subQ1=sQuery(id+"F0.wireOp",EDGE,"E25.1");var subQ2=sQuery(id+"F0.wireOp",EDGE,"E25.2");var subQ3=sQuery(id+"F0.wireOp",EDGE,"E25.3");var subQ4=sQuery(id+"F0.wireOp",EDGE,"E25.4");var subQ5=sQuery(id+"F0.wireOp",EDGE,"E25.5");var subQ6=sQuery(id+"F0.wireOp",EDGE,"E25.6");var subQ7=sQuery(id+"F0.wireOp",EDGE,"E25.7");Q4=makeQuery(id+"F8.boolean.opBoolean","INTERSECT",EDGE,{"derivedFrom":[makeQuery(id+"F5.boolean.opBoolean","SPLIT",FACE,{"disambiguationData":[TD([makeQuery(id+"F2.opExtrude","SWEPT_FACE",FACE,{"disambiguationData":[OSD([subQ0])]})])],"derivedFrom":makeQuery(id+"F3.boolean.opBoolean","COPY",FACE,{"derivedFrom":makeQuery(id+"F3.opExtrude","CAP_FACE",FACE,{"disambiguationData":[OSD([subQ0,subQ1,subQ2,subQ3,subQ4,subQ5,subQ6,subQ7])],"isStart":false})})}),makeQuery(id+"F8.opExtrude","SWEPT_FACE",FACE,{"disambiguationData":[OSD([sQuery(id+"F7.wireOp",EDGE,"E67")])]})]});}
            var Q5;
            Q5=makeQuery(id+"F8.boolean.opBoolean","INTERSECT",EDGE,{"disambiguationData":[OD(0.0)],"derivedFrom":[makeQuery(id+"F5.opExtrude","SWEPT_FACE",FACE,{"disambiguationData":[OSD([sQuery(id+"F4.wireOp",EDGE,"E30")])]}),makeQuery(id+"F8.opExtrude","SWEPT_FACE",FACE,{"disambiguationData":[OSD([sQuery(id+"F7.wireOp",EDGE,"E67")])]})]});
            fillet(context, id + "F14", {"entities" : qUnion([Q0, Q1, Q2, Q3, Q4, Q5]), "radius" : 3 * mm, "tangentPropagation" : true, "allowEdgeOverflow" : false});
        }
        {
            var Q0;
            Q0=makeQuery(id+"F1.opExtrude","CAP_EDGE",EDGE,{"disambiguationData":[OSD([sQuery(id+"F0.wireOp",EDGE,"E1.bottom")])],"isStart":false});
            fillet(context, id + "F15", {"entities" : qUnion([Q0]), "radius" : 2 * mm, "tangentPropagation" : true, "allowEdgeOverflow" : false});
        }
        {
            var Q0;
            {var subQ0=sQuery(id+"F0.wireOp",EDGE,"E22.filletArc");var subQ1=sQuery(id+"F0.wireOp",EDGE,"E7");var subQ2=sQuery(id+"F0.wireOp",EDGE,"E6");var subQ3=sQuery(id+"F0.wireOp",EDGE,"E5");var subQ4=sQuery(id+"F0.wireOp",EDGE,"E4");var subQ5=sQuery(id+"F0.wireOp",EDGE,"E1.bottom");var subQ6=sQuery(id+"F0.wireOp",EDGE,"E21.filletArc");var subQ7=sQuery(id+"F0.wireOp",EDGE,"E1.top");var subQ8=sQuery(id+"F0.wireOp",EDGE,"E1.left");var subQ9=sQuery(id+"F0.wireOp",EDGE,"E1.right");var subQ10=sQuery(id+"F0.wireOp",EDGE,"E23.filletArc");var subQ11=sQuery(id+"F0.wireOp",EDGE,"E24.filletArc");Q0=makeQuery(id+"F2.boolean.opBoolean","SPLIT",FACE,{"disambiguationData":[TD([makeQuery(id+"F1.opExtrude","SWEPT_FACE",FACE,{"disambiguationData":[OSD([subQ5])]})])],"derivedFrom":makeQuery(id+"F1.opExtrude","CAP_FACE",FACE,{"disambiguationData":[OSD([subQ5,subQ7,subQ8,subQ9,subQ4,subQ3,subQ2,subQ1,subQ6,subQ0,subQ10,subQ11])],"isStart":true})});}
            var sketch = newSketch(context, id + "F16", { "sketchPlane" : qUnion([Q0])});
            skLineSegment(sketch, "E79.0", {"start": v(-70, 90) * mm, "end": v(70, 90) * mm});
            skArc(sketch, "E79.1", {"start": v(-70, 90) * mm, "mid": v(-77.07, 87.07) * mm, "end": v(-80, 80) * mm});
            skLineSegment(sketch, "E79.2", {"start": v(-80, -80) * mm, "end": v(-80, 80) * mm});
            skArc(sketch, "E79.3", {"start": v(80, 80) * mm, "mid": v(77.07, 87.07) * mm, "end": v(70, 90) * mm});
            skLineSegment(sketch, "E79.4", {"start": v(80, -80) * mm, "end": v(80, 80) * mm});
            skCircle(sketch, "E79.5", {"center": v(60, 67.5) * mm, "radius": 4 * mm});
            skCircle(sketch, "E79.6", {"center": v(-60, 67.5) * mm, "radius": 4 * mm});
            skArc(sketch, "E79.7", {"start": v(-80, -80) * mm, "mid": v(-77.07, -87.07) * mm, "end": v(-70, -90) * mm});
            skLineSegment(sketch, "E79.8", {"start": v(-70, -90) * mm, "end": v(70, -90) * mm});
            skArc(sketch, "E79.9", {"start": v(70, -90) * mm, "mid": v(77.07, -87.07) * mm, "end": v(80, -80) * mm});
            skCircle(sketch, "E79.10", {"center": v(60, -67.5) * mm, "radius": 4 * mm});
            skCircle(sketch, "E79.11", {"center": v(-60, -67.5) * mm, "radius": 4 * mm});
            skArc(sketch, "E79.12", {"start": v(-56.15, -48.18) * mm, "mid": v(0, -67.5) * mm, "end": v(56.15, -48.18) * mm});
            skArc(sketch, "E79.13", {"start": v(-60, -40.3) * mm, "mid": v(-58.99, -44.68) * mm, "end": v(-56.15, -48.18) * mm});
            skLineSegment(sketch, "E79.14", {"start": v(-60, 40.3) * mm, "end": v(-60, -40.3) * mm});
            skArc(sketch, "E79.15", {"start": v(56.15, -48.18) * mm, "mid": v(58.99, -44.68) * mm, "end": v(60, -40.3) * mm});
            skLineSegment(sketch, "E79.16", {"start": v(60, 40.3) * mm, "end": v(60, -40.3) * mm});
            skArc(sketch, "E79.17", {"start": v(56.15, 48.18) * mm, "mid": v(0, 67.5) * mm, "end": v(-56.15, 48.18) * mm});
            skArc(sketch, "E79.18", {"start": v(60, 40.3) * mm, "mid": v(58.99, 44.68) * mm, "end": v(56.15, 48.18) * mm});
            skArc(sketch, "E79.19", {"start": v(-56.15, 48.18) * mm, "mid": v(-58.99, 44.68) * mm, "end": v(-60, 40.3) * mm});
            skLineSegment(sketch, "E80", {"start": v(-33, 90) * mm, "end": v(-15, 108) * mm});
            skLineSegment(sketch, "E81", {"start": v(-15, 108) * mm, "end": v(-15, 120) * mm});
            skArc(sketch, "E82", {"start": v(15, 120) * mm, "mid": v(0, 135) * mm, "end": v(-15, 120) * mm});
            skLineSegment(sketch, "E83", {"start": v(15, 120) * mm, "end": v(15, 108) * mm});
            skLineSegment(sketch, "E84", {"start": v(15, 108) * mm, "end": v(33, 90) * mm});
            skLineSegment(sketch, "E85", {"start": v(0, 0) * mm, "end": v(0, 120) * mm, "construction": true});
            skCircle(sketch, "E86", {"center": v(0, 120) * mm, "radius": 6 * mm});
            skLineSegment(sketch, "E87", {"start": v(-80, 0) * mm, "end": v(80, 0) * mm, "construction": true});
            skLineSegment(sketch, "E88.MirrorCS", {"start": v(-33, -90) * mm, "end": v(-15, -108) * mm});
            skCircle(sketch, "E89.MirrorC", {"center": v(0, -120) * mm, "radius": 6 * mm});
            skLineSegment(sketch, "E90.MirrorCS", {"start": v(15, -108) * mm, "end": v(33, -90) * mm});
            skArc(sketch, "E91.MirrorCS", {"start": v(15, -120) * mm, "mid": v(0, -135) * mm, "end": v(-15, -120) * mm});
            skLineSegment(sketch, "E92.MirrorCS", {"start": v(15, -120) * mm, "end": v(15, -108) * mm});
            skLineSegment(sketch, "E93.MirrorCS", {"start": v(-15, -108) * mm, "end": v(-15, -120) * mm});
            skSolve(sketch);
        }
        {
            var Q0;
            Q0 = qSketchRegion(id + "F16", true);
            var Q1;
            Q1=makeQuery(id+"F2.opExtrude","CAP_FACE",FACE,{"disambiguationData":[OSD([sQuery(id+"F0.wireOp",EDGE,"E12"),sQuery(id+"F0.wireOp",EDGE,"E13"),sQuery(id+"F0.wireOp",EDGE,"E14"),sQuery(id+"F0.wireOp",EDGE,"E15"),sQuery(id+"F0.wireOp",EDGE,"E17.filletArc"),sQuery(id+"F0.wireOp",EDGE,"E18.filletArc"),sQuery(id+"F0.wireOp",EDGE,"E19.filletArc"),sQuery(id+"F0.wireOp",EDGE,"E20.filletArc"),sQuery(id+"F0.wireOp",EDGE,"E25.0"),sQuery(id+"F0.wireOp",EDGE,"E25.1"),sQuery(id+"F0.wireOp",EDGE,"E25.2"),sQuery(id+"F0.wireOp",EDGE,"E25.3"),sQuery(id+"F0.wireOp",EDGE,"E25.4"),sQuery(id+"F0.wireOp",EDGE,"E25.5"),sQuery(id+"F0.wireOp",EDGE,"E25.6"),sQuery(id+"F0.wireOp",EDGE,"E25.7")])],"isStart":false});
            extrude(context, id + "F17", {"entities" : qUnion([Q0]), "endBound" : BoundingType.UP_TO_SURFACE, "endBoundEntityFace" : qUnion([Q1]), "depth" : 25 * mm});
        }
    });
